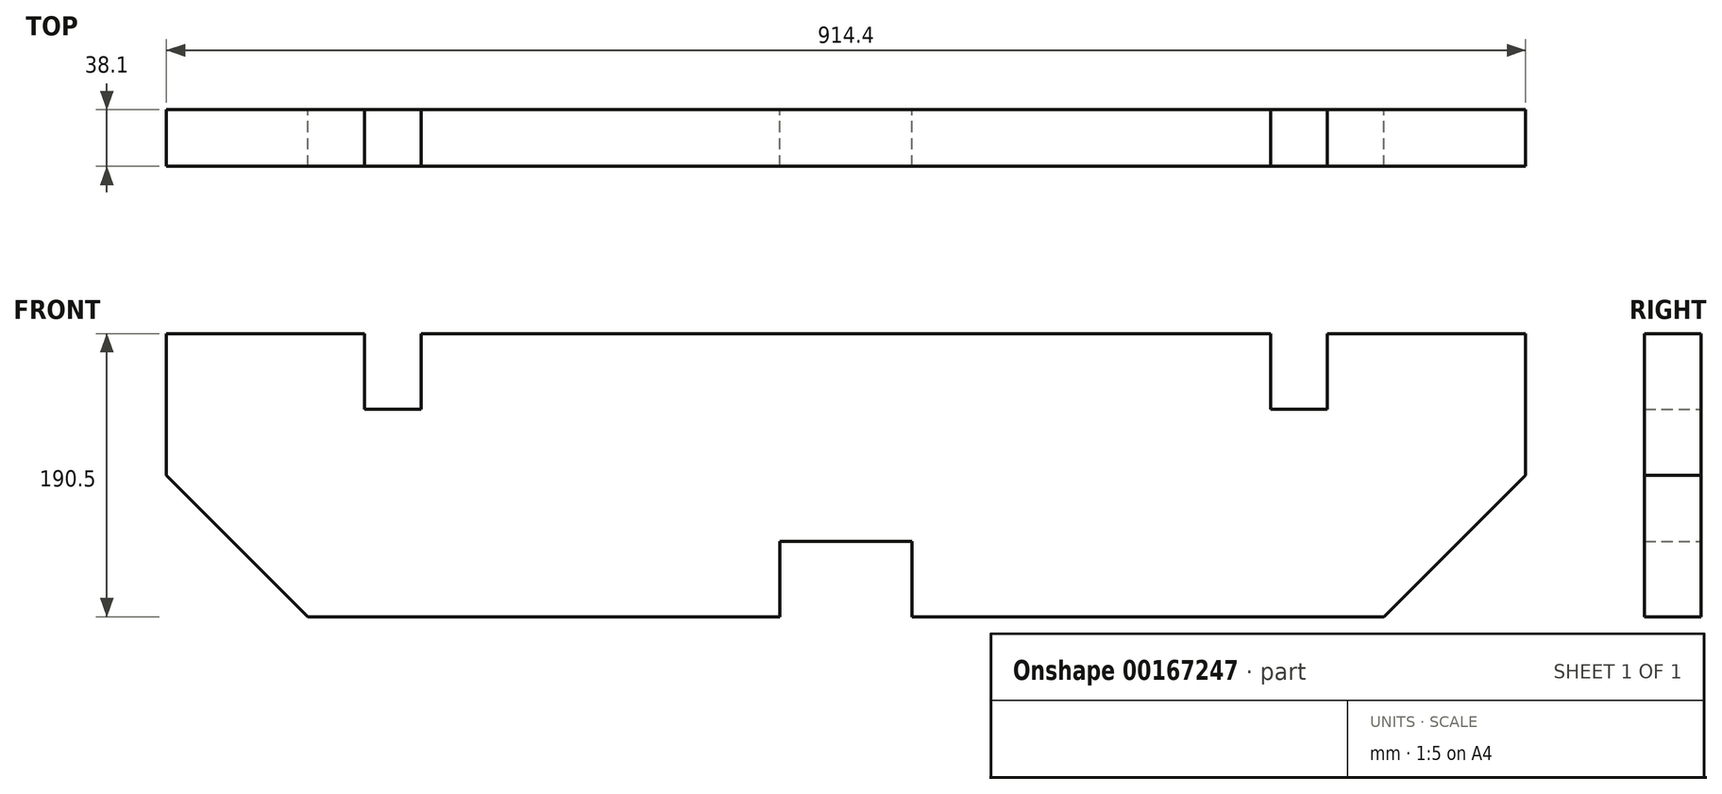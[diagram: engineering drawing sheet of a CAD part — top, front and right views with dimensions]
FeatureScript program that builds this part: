
annotation { "Feature Type Name" : "Feature", "Feature Type Description" : "" }
export const myFeature = defineFeature(function(context is Context, id is Id, definition is map)
    precondition{}
    {
        {
            var Q0;
            Q0=qCreatedBy(makeId("Front.planeOp"),FACE);
            var sketch = newSketch(context, id + "F0", { "sketchPlane" : qUnion([Q0])});
            skLineSegment(sketch, "E0.bottom", {"start": v(0, 0) * mm, "end": v(914.4, 0) * mm});
            skLineSegment(sketch, "E0.top", {"start": v(0, 190.5) * mm, "end": v(914.4, 190.5) * mm});
            skLineSegment(sketch, "E0.left", {"start": v(0, 0) * mm, "end": v(0, 190.5) * mm});
            skLineSegment(sketch, "E0.right", {"start": v(914.4, 0) * mm, "end": v(914.4, 190.5) * mm});
            skLineSegment(sketch, "E1", {"start": v(412.75, 0) * mm, "end": v(412.75, 50.8) * mm});
            skLineSegment(sketch, "E2", {"start": v(412.75, 50.8) * mm, "end": v(501.65, 50.8) * mm});
            skLineSegment(sketch, "E3", {"start": v(501.65, 50.8) * mm, "end": v(501.65, 0) * mm});
            skLineSegment(sketch, "E4", {"start": v(412.75, 50.8) * mm, "end": v(0, 50.8) * mm, "construction": true});
            skLineSegment(sketch, "E5", {"start": v(501.65, 50.8) * mm, "end": v(914.4, 50.8) * mm, "construction": true});
            skLineSegment(sketch, "E6", {"start": v(184.03, 190.5) * mm, "end": v(184.03, 95.25) * mm, "construction": true});
            skLineSegment(sketch, "E7", {"start": v(184.03, 95.25) * mm, "end": v(184.03, 0) * mm, "construction": true});
            skLineSegment(sketch, "E8", {"start": v(0, 95.25) * mm, "end": v(95.25, 0) * mm});
            skLineSegment(sketch, "E9", {"start": v(914.4, 95.25) * mm, "end": v(819.15, 0) * mm});
            skLineSegment(sketch, "E10", {"start": v(742.95, 190.5) * mm, "end": v(742.95, 139.7) * mm});
            skLineSegment(sketch, "E11", {"start": v(742.95, 139.7) * mm, "end": v(781.05, 139.7) * mm});
            skLineSegment(sketch, "E12", {"start": v(781.05, 139.7) * mm, "end": v(781.05, 190.5) * mm});
            skLineSegment(sketch, "E13", {"start": v(133.35, 190.5) * mm, "end": v(133.35, 139.7) * mm});
            skLineSegment(sketch, "E14", {"start": v(133.35, 139.7) * mm, "end": v(171.45, 139.7) * mm});
            skLineSegment(sketch, "E15", {"start": v(171.45, 139.7) * mm, "end": v(171.45, 190.5) * mm});
            skLineSegment(sketch, "E16", {"start": v(133.35, 139.7) * mm, "end": v(0, 139.7) * mm, "construction": true});
            skLineSegment(sketch, "E17", {"start": v(171.45, 139.7) * mm, "end": v(742.95, 139.7) * mm, "construction": true});
            skLineSegment(sketch, "E18", {"start": v(742.95, 139.7) * mm, "end": v(781.05, 139.7) * mm, "construction": true});
            skLineSegment(sketch, "E19", {"start": v(781.05, 139.7) * mm, "end": v(914.4, 139.7) * mm, "construction": true});
            skSolve(sketch);
        }
        {
            var Q0;
            {var subQ10=sQuery(id+"F0.wireOp",EDGE,"E1");Q0=makeQuery(id+"F0.imprint","IMPRINT",FACE,{"disambiguationData":[TD([[makeQuery(id+"F0.imprint","IMPRINT",EDGE,{"derivedFrom":subQ10}),1.0]])]});}
            extrude(context, id + "F1", {"entities" : qUnion([Q0]), "depth" : 38.1 * mm});
        }
    });
